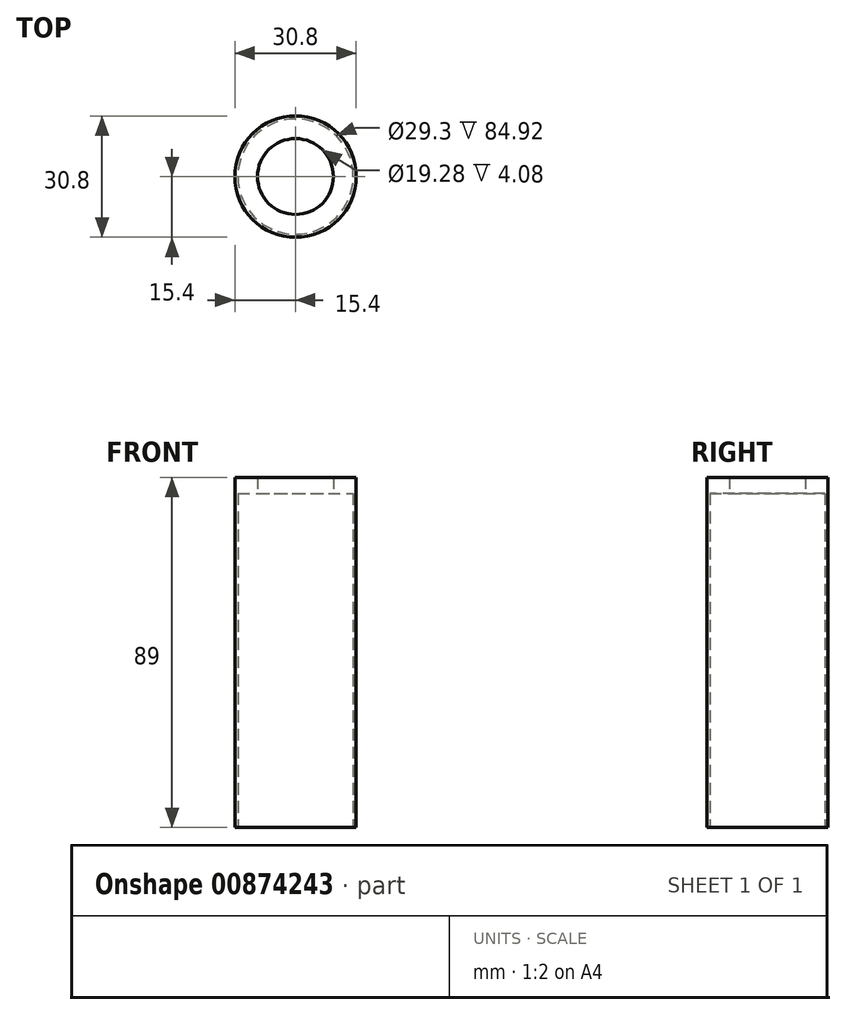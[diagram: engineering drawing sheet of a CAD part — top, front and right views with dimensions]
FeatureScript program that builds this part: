
annotation { "Feature Type Name" : "Feature", "Feature Type Description" : "" }
export const myFeature = defineFeature(function(context is Context, id is Id, definition is map)
    precondition{}
    {
        {
            var Q0;
            Q0=qCreatedBy(makeId("Top.planeOp"),FACE);
            var sketch = newSketch(context, id + "F0", { "sketchPlane" : qUnion([Q0])});
            skCircle(sketch, "E0", {"center": v(0, 0) * mm, "radius": 15.4 * mm});
            skCircle(sketch, "E1", {"center": v(0, 0) * mm, "radius": 14.65 * mm});
            skSolve(sketch);
        }
        {
            var Q0;
            {var subQ0=sQuery(id+"F0.wireOp",EDGE,"ZYTGvfPV-ei2S-3O7y-2hYI-zFQv9VdfXTHt");Q0=makeQuery(id+"F0.imprint","IMPRINT",FACE,{"disambiguationData":[TD([[makeQuery(id+"F0.imprint","IMPRINT",EDGE,{"derivedFrom":subQ0}),1.0]])]});}
            var Q1;
            Q1=makeQuery(id+"F0.imprint","IMPRINT",FACE,{"disambiguationData":[TD([[makeQuery(id+"F0.imprint","IMPRINT",EDGE,{"derivedFrom":sQuery(id+"F0.wireOp",EDGE,"E0")}),1.0]])]});
            extrude(context, id + "F1", {"entities" : qUnion([Q0, Q1]), "depth" : 89 * mm, "offsetDistance" : 25.4 * mm});
        }
        {
            var Q0;
            Q0=qCreatedBy(makeId("Front.planeOp"),FACE);
            var sketch = newSketch(context, id + "F2", { "sketchPlane" : qUnion([Q0])});
            skLineSegment(sketch, "E2", {"start": v(15.4, 89) * mm, "end": v(15.4, 0) * mm});
            skLineSegment(sketch, "E3", {"start": v(-15.4, 0) * mm, "end": v(-15.4, 89) * mm});
            skLineSegment(sketch, "E4", {"start": v(14.65, 89) * mm, "end": v(14.65, 0) * mm});
            skLineSegment(sketch, "E5", {"start": v(-14.65, 0) * mm, "end": v(-14.65, 89) * mm});
            skLineSegment(sketch, "E6.bottom", {"start": v(14.65, 89) * mm, "end": v(9.64, 89) * mm});
            skLineSegment(sketch, "E6.top", {"start": v(14.65, 84.92) * mm, "end": v(9.64, 84.92) * mm});
            skLineSegment(sketch, "E6.left", {"start": v(14.65, 89) * mm, "end": v(14.65, 84.92) * mm});
            skLineSegment(sketch, "E6.right", {"start": v(9.64, 89) * mm, "end": v(9.64, 84.92) * mm});
            skLineSegment(sketch, "E7", {"start": v(0, 0) * mm, "end": v(0, 137.23) * mm, "construction": true});
            skSolve(sketch);
        }
        {
            var Q0;
            Q0=makeQuery(id+"F2.imprint","IMPRINT",FACE,{"disambiguationData":[TD([[makeQuery(id+"F2.imprint","IMPRINT",EDGE,{"derivedFrom":sQuery(id+"F2.wireOp",EDGE,"E6.bottom")}),1.0]])]});
            var Q1;
            Q1=sQuery(id+"F2.wireOp",EDGE,"E7");
            revolve(context, id + "F3", {"operationType" : NewBodyOperationType.ADD, "surfaceOperationType" : NewSurfaceOperationType.NEW, "entities" : qUnion([Q0]), "axis" : qUnion([Q1]), "revolveType" : RevolveType.FULL});
        }
    });
